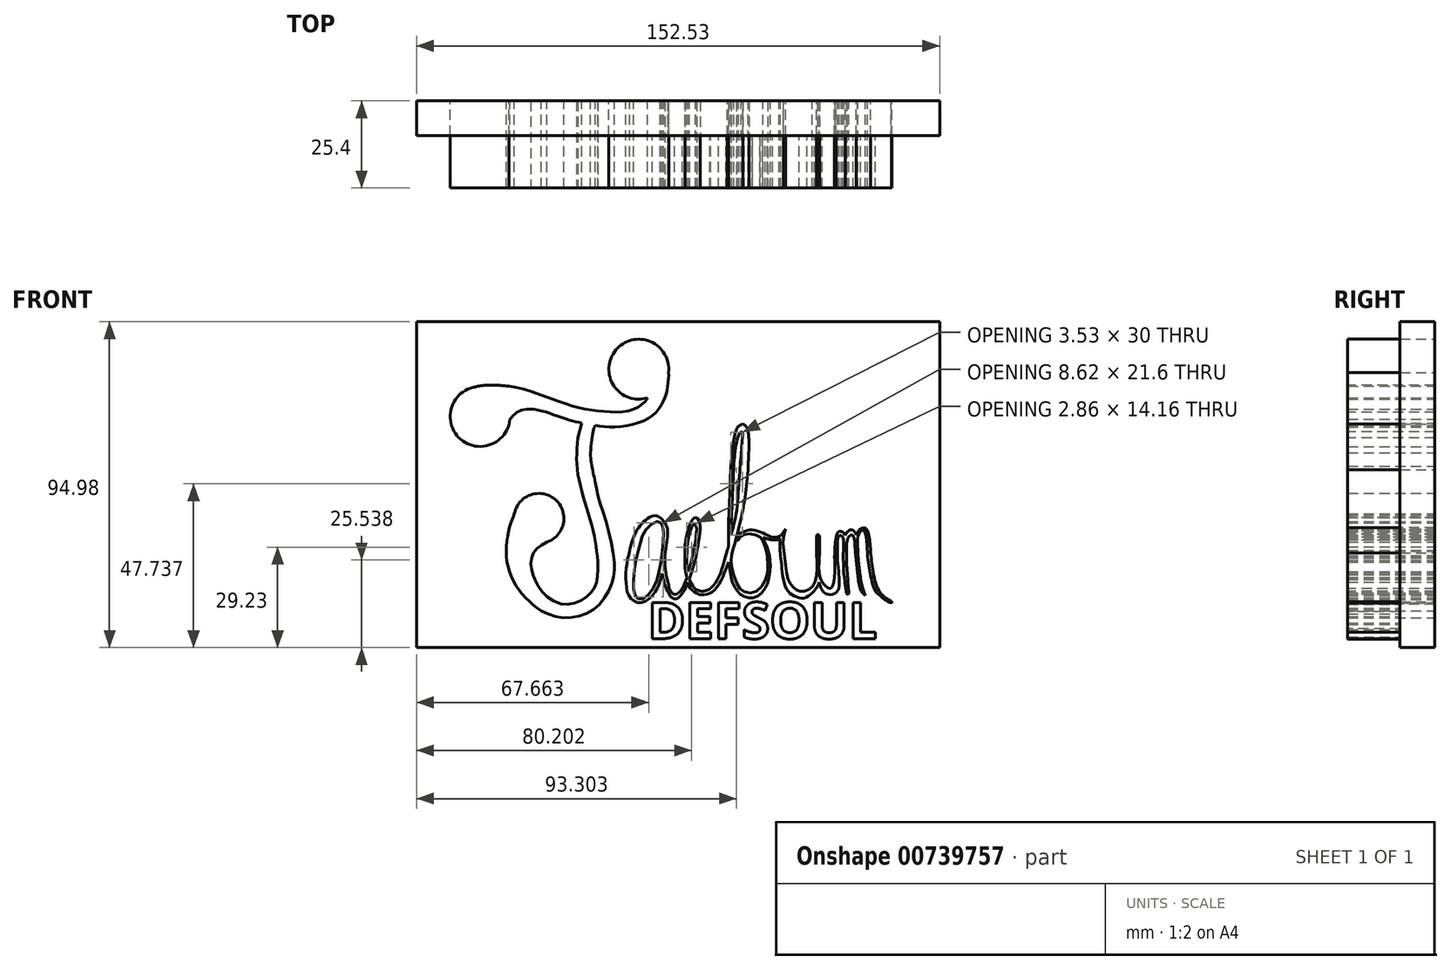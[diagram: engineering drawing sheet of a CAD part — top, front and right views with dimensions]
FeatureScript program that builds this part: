
annotation { "Feature Type Name" : "Feature", "Feature Type Description" : "" }
export const myFeature = defineFeature(function(context is Context, id is Id, definition is map)
    precondition{}
    {
        {
            var Q0;
            Q0=qCreatedBy(makeId("Front.planeOp"),FACE);
            var sketch = newSketch(context, id + "F0", { "sketchPlane" : qUnion([Q0])});
            skCircle(sketch, "E0", {"center": v(-57.58, 28.36) * mm, "radius": 8.73 * mm});
            skFitSpline(sketch, "E1", {"points": [v(-55.56, 36.85) * mm, v(-47.7, 37) * mm, v(-31.6, 31.7) * mm, v(-22.02, 29.91) * mm, v(-13.64, 30.17) * mm, v(-9.36, 32.82) * mm, v(-8.72, 33.82) * mm], "startDerivative": vector(35.06, 6.54) * mm, "endDerivative": vector(6.2, 15.4) * mm});
            skFitSpline(sketch, "E2", {"points": [v(-48.89, 27.54) * mm, v(-46.41, 29.83) * mm, v(-41.2, 30.34) * mm, v(-31.95, 27.43) * mm, v(-26.13, 26.15) * mm, v(-19.29, 25.3) * mm, v(-8.72, 27.69) * mm, v(-4.23, 32.65) * mm, v(-2.86, 37.36) * mm, v(-2.66, 41.14) * mm], "startDerivative": vector(25.7, 30.9) * mm, "endDerivative": vector(-3.63, 27.27) * mm});
            skCircle(sketch, "E3", {"center": v(-11.33, 42.15) * mm, "radius": 8.73 * mm});
            skCircle(sketch, "E4", {"center": v(-40.44, -1.35) * mm, "radius": 7.28 * mm});
            skFitSpline(sketch, "E5", {"points": [v(-47.6, 0) * mm, v(-48.78, -3.23) * mm, v(-49.93, -9.63) * mm, v(-49.07, -16.75) * mm, v(-45.3, -23.43) * mm, v(-39.82, -28.32) * mm], "startDerivative": vector(-8.2, -19.78) * mm, "endDerivative": vector(26.77, -20.88) * mm});
            skFitSpline(sketch, "E6", {"points": [v(-39.82, -28.32) * mm, v(-33.9, -30.27) * mm, v(-27.59, -29.45) * mm, v(-22.3, -25.9) * mm, v(-19.14, -20) * mm, v(-18.43, -15.1) * mm, v(-20.16, -4.83) * mm, v(-23, 4.53) * mm, v(-24.03, 9.11) * mm], "startDerivative": vector(48.48, -21.15) * mm, "endDerivative": vector(-7.56, 40.7) * mm});
            skFitSpline(sketch, "E7", {"points": [v(-38.08, -8.25) * mm, v(-41.75, -11.04) * mm, v(-42.75, -14.8) * mm, v(-41.75, -18.87) * mm, v(-38.37, -23.96) * mm, v(-31.66, -26.45) * mm, v(-26.14, -23.8) * mm, v(-23.76, -20.5) * mm, v(-23.27, -13.83) * mm], "startDerivative": vector(-36.38, -20.88) * mm, "endDerivative": vector(-0.7, 52.44) * mm});
            skFitSpline(sketch, "E8", {"points": [v(-23.27, -13.83) * mm, v(-24.45, -5.8) * mm, v(-27.36, 4.53) * mm, v(-29.33, 13.72) * mm, v(-29.07, 22.1) * mm], "startDerivative": vector(-3.51, 32.96) * mm, "endDerivative": vector(3.07, 34.87) * mm});
            skFitSpline(sketch, "E9", {"points": [v(-29.07, 22.1) * mm, v(-28.21, 25.28) * mm, v(-27.9, 26.47) * mm], "startDerivative": vector(1.55, 5.76) * mm, "endDerivative": vector(0.75, 2.81) * mm});
            skFitSpline(sketch, "E10", {"points": [v(-24.03, 9.11) * mm, v(-24.89, 13.55) * mm, v(-25.37, 17.66) * mm, v(-24.65, 23.95) * mm, v(-24.03, 25.75) * mm], "startDerivative": vector(-3.38, 17.42) * mm, "endDerivative": vector(3.65, 8.4) * mm});
            skFitSpline(sketch, "E11", {"points": [v(-4.9, -2.66) * mm, v(-6.19, -2.3) * mm, v(-9.36, -4.75) * mm, v(-10.8, -8.2) * mm, v(-12.16, -13.83) * mm, v(-12.88, -21.51) * mm, v(-12.09, -24.25) * mm, v(-10.58, -24.97) * mm, v(-7.63, -22.38) * mm, v(-5.54, -17.41) * mm, v(-4.23, -8.78) * mm, v(-4.23, -4.25) * mm, v(-4.9, -2.66) * mm]});
            skFitSpline(sketch, "E12", {"points": [v(-5.1, -1.08) * mm, v(-6.27, -0.56) * mm, v(-8.03, -1) * mm, v(-10.98, -3.49) * mm, v(-12.86, -6.87) * mm, v(-14, -10.76) * mm], "startDerivative": vector(-8.28, 5.07) * mm, "endDerivative": vector(-4.26, -16.62) * mm});
            skFitSpline(sketch, "E13", {"points": [v(-14, -10.76) * mm, v(-14.9, -15.18) * mm, v(-15.04, -20.5) * mm, v(-14, -24.25) * mm, v(-11.3, -25.9) * mm, v(-7.63, -24.25) * mm, v(-5.54, -20.72) * mm, v(-4.53, -17.41) * mm], "startDerivative": vector(-6.8, -28.21) * mm, "endDerivative": vector(6.65, 24.7) * mm});
            skFitSpline(sketch, "E14", {"points": [v(-5.1, -1.08) * mm, v(-3.24, -3.45) * mm, v(-3.02, -7.27) * mm, v(-3.74, -13.24) * mm, v(-2.8, -20) * mm], "startDerivative": vector(11.2, -10.92) * mm, "endDerivative": vector(6.02, -22.76) * mm});
            skFitSpline(sketch, "E15", {"points": [v(-2.8, -20) * mm, v(-2.01, -22.6) * mm, v(-0.72, -23.53) * mm, v(1, -22.23) * mm, v(2.52, -19.14) * mm], "startDerivative": vector(2.08, -10.74) * mm, "endDerivative": vector(4.4, 11.1) * mm});
            skFitSpline(sketch, "E16", {"points": [v(-4.53, -17.41) * mm, v(-3.78, -20.37) * mm, v(-2.8, -22.82) * mm, v(-1.9, -24.25) * mm, v(-0.49, -24.84) * mm, v(0.82, -23.88) * mm, v(2.54, -21.21) * mm, v(2.93, -20) * mm], "startDerivative": vector(3.81, -17.35) * mm, "endDerivative": vector(2.15, 9.7) * mm});
            skFitSpline(sketch, "E17", {"points": [v(2.52, -19.14) * mm, v(2.78, -18.5) * mm], "startDerivative": vector(0.26, 0.64) * mm, "endDerivative": vector(0.26, 0.64) * mm});
            skFitSpline(sketch, "E18", {"points": [v(2.78, -18.5) * mm, v(2.35, -17.05) * mm, v(2.11, -14.4) * mm, v(2.13, -11.06) * mm, v(2.2, -9.66) * mm], "startDerivative": vector(-2.3, 6.45) * mm, "endDerivative": vector(0.39, 6.1) * mm});
            skFitSpline(sketch, "E19", {"points": [v(2.2, -9.66) * mm, v(2.2, -8.52) * mm, v(3.44, -3.59) * mm, v(4.74, -1.35) * mm, v(5.7, -1.23) * mm, v(6.53, -3.05) * mm, v(6.4, -6.13) * mm, v(5.65, -10.82) * mm, v(5.26, -12.94) * mm], "startDerivative": vector(-1.12, 10.68) * mm, "endDerivative": vector(-3.09, -16.08) * mm});
            skFitSpline(sketch, "E20", {"points": [v(3.41, -19.07) * mm, v(4.41, -15.96) * mm, v(5.26, -12.94) * mm], "startDerivative": vector(2.04, 6.18) * mm, "endDerivative": vector(1.64, 6.09) * mm});
            skFitSpline(sketch, "E21", {"points": [v(3.41, -19.07) * mm, v(4.9, -21.67) * mm, v(7.44, -22.55) * mm, v(10.55, -20.83) * mm, v(13.15, -15.44) * mm, v(14.42, -10.63) * mm], "startDerivative": vector(6.77, -16.8) * mm, "endDerivative": vector(4.83, 20.57) * mm});
            skFitSpline(sketch, "E22", {"points": [v(2.93, -20) * mm, v(3.41, -21.37) * mm, v(5.26, -23.06) * mm, v(6.44, -23.58) * mm, v(8.43, -23.52) * mm, v(11.28, -21.73) * mm, v(13.82, -16.68) * mm, v(14.82, -14.14) * mm], "startDerivative": vector(2.14, -12.7) * mm, "endDerivative": vector(5.95, 15.05) * mm});
            skFitSpline(sketch, "E23", {"points": [v(3.03, -16.85) * mm, v(2.68, -14.88) * mm, v(2.73, -11.5) * mm, v(3.03, -7.74) * mm, v(4.41, -3.42) * mm, v(5.17, -2.69) * mm], "startDerivative": vector(-2.54, 10.73) * mm, "endDerivative": vector(6.08, 3.92) * mm});
            skFitSpline(sketch, "E24", {"points": [v(3.03, -16.85) * mm, v(3.97, -13.9) * mm, v(5.17, -7.9) * mm, v(5.5, -4.19) * mm, v(5.17, -2.69) * mm], "startDerivative": vector(3.96, 11.02) * mm, "endDerivative": vector(-2.64, 8.1) * mm});
            skFitSpline(sketch, "E25", {"points": [v(14.42, -10.63) * mm, v(14.82, -9.56) * mm, v(14.82, -7.15) * mm, v(14.82, -2.31) * mm], "startDerivative": vector(2.16, 4.38) * mm, "endDerivative": vector(0.16, 11.32) * mm});
            skFitSpline(sketch, "E26", {"points": [v(14.82, -2.31) * mm, v(15.25, 6.48) * mm, v(15.51, 13.63) * mm, v(15.68, 15.77) * mm], "startDerivative": vector(1.16, 20.86) * mm, "endDerivative": vector(0.87, 8.82) * mm});
            skFitSpline(sketch, "E27", {"points": [v(15.68, 15.77) * mm, v(16.1, 19.5) * mm, v(17.4, 25.03) * mm, v(19, 26.12) * mm], "startDerivative": vector(1, 9.76) * mm, "endDerivative": vector(7.17, 2.57) * mm});
            skFitSpline(sketch, "E28", {"points": [v(19, 26.12) * mm, v(19.93, 25.48) * mm, v(20.75, 22.16) * mm, v(20.66, 16.32) * mm, v(20.5, 12.9) * mm], "startDerivative": vector(6.8, -2.85) * mm, "endDerivative": vector(-0.49, -12.18) * mm});
            skFitSpline(sketch, "E29", {"points": [v(20.5, 12.9) * mm, v(19.5, 3.89) * mm, v(18.28, -2.31) * mm, v(15.68, -12.17) * mm], "startDerivative": vector(-2.72, -27.76) * mm, "endDerivative": vector(-7.83, -28.82) * mm});
            skFitSpline(sketch, "E30", {"points": [v(15.68, -12.17) * mm, v(15.68, -14.92) * mm, v(17.45, -20.78) * mm, v(19.33, -22.65) * mm, v(22.78, -22.73) * mm, v(25.55, -19.42) * mm, v(26.23, -16.85) * mm, v(26.23, -13.55) * mm, v(25.87, -10.93) * mm, v(24.76, -7.76) * mm, v(23.5, -6.46) * mm, v(20.15, -5.89) * mm, v(18.5, -6.54) * mm, v(17.81, -7.54) * mm], "startDerivative": vector(-3.16, -31.7) * mm, "endDerivative": vector(-11.45, -21.77) * mm});
            skFitSpline(sketch, "E31", {"points": [v(14.82, -14.14) * mm, v(15.62, -18.66) * mm, v(17.17, -22.3) * mm, v(19.8, -24.24) * mm, v(23.32, -24.02) * mm, v(26.27, -20) * mm, v(26.99, -14.52) * mm, v(26.38, -10.63) * mm, v(24.83, -6.86) * mm], "startDerivative": vector(5, -35.2) * mm, "endDerivative": vector(-14.17, 30.67) * mm});
            skFitSpline(sketch, "E32", {"points": [v(17.81, -7.54) * mm, v(17.64, -7.7) * mm, v(17.28, -7.67) * mm, v(17.17, -7.4) * mm, v(17.37, -6.94) * mm], "startDerivative": vector(-0.63, -0.96) * mm, "endDerivative": vector(0.93, 1.56) * mm});
            skFitSpline(sketch, "E33", {"points": [v(17.37, -6.94) * mm, v(18.22, -5.8) * mm, v(20.18, -4.9) * mm, v(22.39, -4.81) * mm, v(25.25, -5.78) * mm, v(26.8, -6.55) * mm, v(28.65, -6.86) * mm, v(30.37, -6.06) * mm, v(30.8, -5.37) * mm], "startDerivative": vector(6.05, 11.03) * mm, "endDerivative": vector(3.5, 8.22) * mm});
            skFitSpline(sketch, "E34", {"points": [v(24.83, -6.86) * mm, v(26.06, -7.28) * mm, v(27.6, -7.63) * mm, v(28.86, -7.61) * mm, v(29.62, -7.43) * mm], "startDerivative": vector(4.59, -1.63) * mm, "endDerivative": vector(3.53, 1.03) * mm});
            skLineSegment(sketch, "E35", {"start": v(29.62, -7.43) * mm, "end": v(29.9, -7.13) * mm});
            skFitSpline(sketch, "E36", {"points": [v(29.9, -7.13) * mm, v(29.82, -8.2) * mm, v(29.8, -10.08) * mm, v(29.9, -11.35) * mm], "startDerivative": vector(-0.34, -3.32) * mm, "endDerivative": vector(0.36, -3.7) * mm});
            skFitSpline(sketch, "E37", {"points": [v(29.9, -11.35) * mm, v(30.39, -15.89) * mm, v(31.72, -21.9) * mm, v(34.17, -24.02) * mm, v(36.8, -24.6) * mm, v(39.2, -23.12) * mm], "startDerivative": vector(2.01, -19.12) * mm, "endDerivative": vector(13.47, 11.42) * mm});
            skFitSpline(sketch, "E38", {"points": [v(30.8, -5.37) * mm, v(31.45, -4.48) * mm], "startDerivative": vector(0.66, 0.9) * mm, "endDerivative": vector(0.66, 0.9) * mm});
            skFitSpline(sketch, "E39", {"points": [v(31.45, -4.48) * mm, v(30.8, -7.13) * mm, v(31.23, -13.3) * mm, v(32.4, -19.54) * mm, v(34.36, -22.02) * mm, v(36.07, -22.66) * mm, v(38.81, -21.72) * mm, v(40.57, -17.83) * mm, v(40.52, -11.35) * mm, v(40.44, -6.7) * mm], "startDerivative": vector(-9.47, -26.13) * mm, "endDerivative": vector(0, 37.12) * mm});
            skFitSpline(sketch, "E40", {"points": [v(39.2, -23.12) * mm, v(40.65, -21.34) * mm, v(41.2, -20) * mm], "startDerivative": vector(2.97, 3.25) * mm, "endDerivative": vector(0.96, 3) * mm});
            skFitSpline(sketch, "E41", {"points": [v(40.44, -6.7) * mm, v(40.54, -6.28) * mm, v(40.9, -6.1) * mm, v(41.26, -6.26) * mm, v(41.33, -7.02) * mm], "startDerivative": vector(0.17, 1.99) * mm, "endDerivative": vector(-0.16, -2.84) * mm});
            skFitSpline(sketch, "E42", {"points": [v(41.33, -7.02) * mm, v(41.33, -11.8) * mm, v(41.33, -17.83) * mm, v(42.71, -20.6) * mm, v(44.4, -21.77) * mm, v(45.46, -20) * mm, v(45.77, -12.31) * mm], "startDerivative": vector(0.62, -24.76) * mm, "endDerivative": vector(-0.76, 37.6) * mm});
            skFitSpline(sketch, "E43", {"points": [v(41.2, -20) * mm, v(42.1, -22.23) * mm, v(43.78, -23.5) * mm, v(46.27, -22.9) * mm, v(47.14, -20) * mm, v(46.58, -13.55) * mm], "startDerivative": vector(4.1, -13.6) * mm, "endDerivative": vector(-3.08, 24.18) * mm});
            skFitSpline(sketch, "E44", {"points": [v(45.77, -12.31) * mm, v(45.97, -8.42) * mm, v(46.22, -6.83) * mm], "startDerivative": vector(0.23, 7.1) * mm, "endDerivative": vector(0.72, 3.6) * mm});
            skFitSpline(sketch, "E45", {"points": [v(15.42, -6.26) * mm, v(17, -0.44) * mm, v(18.02, 11) * mm, v(18.56, 17.77) * mm], "startDerivative": vector(6.01, 17.67) * mm, "endDerivative": vector(1.77, 19.83) * mm});
            skFitSpline(sketch, "E46", {"points": [v(18.56, 17.77) * mm, v(18.91, 22.16) * mm, v(18.91, 23.57) * mm, v(18.56, 23.88) * mm, v(17.74, 22.76) * mm, v(16.8, 18.44) * mm, v(16.32, 13.9) * mm], "startDerivative": vector(1.59, 21.96) * mm, "endDerivative": vector(-1.8, -19.48) * mm});
            skFitSpline(sketch, "E47", {"points": [v(16.32, 13.9) * mm, v(15.42, -6.26) * mm], "startDerivative": vector(-0.9, -20.17) * mm, "endDerivative": vector(-0.9, -20.17) * mm});
            skFitSpline(sketch, "E48", {"points": [v(46.58, -13.55) * mm, v(46.58, -9.55) * mm, v(46.87, -6.72) * mm, v(47.74, -6.26) * mm], "startDerivative": vector(0.06, 9.29) * mm, "endDerivative": vector(4.72, 1.1) * mm});
            skFitSpline(sketch, "E49", {"points": [v(46.22, -6.83) * mm, v(46.87, -5.27) * mm, v(48, -5.27) * mm, v(48.86, -6.26) * mm], "startDerivative": vector(1.1, 5.22) * mm, "endDerivative": vector(2.23, -3.6) * mm});
            skFitSpline(sketch, "E50", {"points": [v(47.74, -6.26) * mm, v(48.25, -7.13) * mm, v(48.3, -11.28) * mm, v(48.45, -17.83) * mm], "startDerivative": vector(3.33, -3.8) * mm, "endDerivative": vector(0.66, -14.56) * mm});
            skFitSpline(sketch, "E51", {"points": [v(48.45, -17.83) * mm, v(49.16, -22.7) * mm, v(49.37, -23.4) * mm, v(49.6, -23.5) * mm, v(49.85, -23.2) * mm, v(49.77, -21.9) * mm, v(49.68, -19.88) * mm, v(49.65, -19.22) * mm], "startDerivative": vector(2.83, -20.12) * mm, "endDerivative": vector(-0.38, 5.14) * mm});
            skFitSpline(sketch, "E52", {"points": [v(48.86, -6.26) * mm, v(49.9, -4.9) * mm, v(51.16, -4.81) * mm, v(52.1, -6.26) * mm], "startDerivative": vector(2.5, 4.65) * mm, "endDerivative": vector(2.15, -5.16) * mm});
            skFitSpline(sketch, "E53", {"points": [v(52.1, -6.26) * mm, v(52.8, -4.9) * mm, v(53.88, -4.16) * mm, v(55.01, -4.4) * mm, v(55.93, -7.29) * mm, v(56.3, -11.44) * mm], "startDerivative": vector(3.45, 8.55) * mm, "endDerivative": vector(0.98, -14.7) * mm});
            skFitSpline(sketch, "E54", {"points": [v(49.27, -10.87) * mm, v(49.4, -8.04) * mm, v(50.3, -6.34) * mm, v(51.15, -6.34) * mm, v(51.69, -9.34) * mm, v(51.96, -12.5) * mm], "startDerivative": vector(-0.45, 13.01) * mm, "endDerivative": vector(1.26, -12.43) * mm});
            skFitSpline(sketch, "E55", {"points": [v(52.58, -12.5) * mm, v(52.58, -12.09) * mm, v(52.51, -9.75) * mm, v(52.42, -7.5) * mm, v(53.12, -5.32) * mm, v(53.93, -4.81) * mm, v(54.38, -4.9) * mm, v(55.21, -9.28) * mm, v(55.4, -12.5) * mm], "startDerivative": vector(0.03, 5.32) * mm, "endDerivative": vector(0.51, -16.5) * mm});
            skFitSpline(sketch, "E56", {"points": [v(49.27, -10.87) * mm, v(49.27, -14.66) * mm, v(49.65, -19.22) * mm], "startDerivative": vector(-0.17, -7.77) * mm, "endDerivative": vector(0.9, -8.91) * mm});
            skFitSpline(sketch, "E57", {"points": [v(51.96, -12.5) * mm, v(52.53, -18.05) * mm, v(53.38, -22.22) * mm, v(54.7, -23.85) * mm], "startDerivative": vector(1.4, -13.9) * mm, "endDerivative": vector(6, -5.54) * mm});
            skFitSpline(sketch, "E58", {"points": [v(52.58, -12.5) * mm, v(53.04, -16.84) * mm, v(53.92, -21.7) * mm, v(54.7, -23.85) * mm], "startDerivative": vector(1.07, -11.57) * mm, "endDerivative": vector(3.13, -7.25) * mm});
            skFitSpline(sketch, "E59", {"points": [v(55.4, -12.5) * mm, v(56.34, -18.42) * mm, v(57.93, -22.78) * mm, v(61.27, -25.58) * mm, v(62.2, -25.94) * mm], "startDerivative": vector(2.9, -19.26) * mm, "endDerivative": vector(6, -1.63) * mm});
            skFitSpline(sketch, "E60", {"points": [v(56.3, -11.44) * mm, v(56.77, -15.6) * mm, v(57.82, -20.43) * mm, v(59.22, -23.14) * mm, v(60.8, -24.61) * mm, v(62.35, -25.58) * mm], "startDerivative": vector(1.64, -17.34) * mm, "endDerivative": vector(10.16, -5.93) * mm});
            skFitSpline(sketch, "E61", {"points": [v(62.2, -25.94) * mm, v(62.41, -25.94) * mm, v(62.53, -25.76) * mm, v(62.35, -25.58) * mm], "startDerivative": vector(0.66, -0.15) * mm, "endDerivative": vector(-0.72, 0.44) * mm});
            skFitSpline(sketch, "E62", {"points": [v(-59.66, 36.83) * mm, v(-55.83, 37.48) * mm, v(-49.15, 37.2) * mm], "startDerivative": vector(8.22, 1.95) * mm, "endDerivative": vector(12.6, -1.08) * mm});
            skSolve(sketch);
        }
        {
            var Q0;
            {var subQ0=sQuery(id+"F0.wireOp",EDGE,"E0");var subQ1=makeQuery(id+"F0.imprint","INTERSECT",VERTEX,{"derivedFrom":[subQ0,sQuery(id+"F0.wireOp",EDGE,"E1")]});Q0=makeQuery(id+"F0.imprint","IMPRINT",FACE,{"disambiguationData":[TD([[makeQuery(id+"F0.imprint","IMPRINT",EDGE,{"disambiguationData":[TD([[subQ1,-1.0]])],"derivedFrom":subQ0}),1.0]])]});}
            var Q1;
            {var subQ1=sQuery(id+"F0.wireOp",EDGE,"E0");var subQ5=sQuery(id+"F0.wireOp",EDGE,"E1");var subQ10=makeQuery(id+"F0.imprint","INTERSECT",VERTEX,{"derivedFrom":[subQ1,subQ5]});Q1=makeQuery(id+"F0.imprint","IMPRINT",FACE,{"disambiguationData":[TD([[makeQuery(id+"F0.imprint","IMPRINT",EDGE,{"disambiguationData":[TD([[subQ10,1.0]])],"derivedFrom":subQ1}),-1.0]])]});}
            var Q2;
            {var subQ0=sQuery(id+"F0.wireOp",EDGE,"E3");var subQ1=makeQuery(id+"F0.imprint","INTERSECT",VERTEX,{"derivedFrom":[sQuery(id+"F0.wireOp",EDGE,"E1"),subQ0]});Q2=makeQuery(id+"F0.imprint","IMPRINT",FACE,{"disambiguationData":[TD([[makeQuery(id+"F0.imprint","IMPRINT",EDGE,{"disambiguationData":[TD([[subQ1,-1.0]])],"derivedFrom":subQ0}),1.0]])]});}
            var Q3;
            {var subQ0=sQuery(id+"F0.wireOp",EDGE,"E1");var subQ1=sQuery(id+"F0.wireOp",EDGE,"E0");var subQ2=makeQuery(id+"F0.imprint","INTERSECT",VERTEX,{"derivedFrom":[subQ1,subQ0]});Q3=makeQuery(id+"F0.imprint","IMPRINT",FACE,{"disambiguationData":[TD([[makeQuery(id+"F0.imprint","IMPRINT",EDGE,{"disambiguationData":[TD([[subQ2,-1.0]])],"derivedFrom":subQ1}),-1.0]])]});}
            var Q4;
            {var subQ0=sQuery(id+"F0.wireOp",EDGE,"E4");var subQ1=makeQuery(id+"F0.imprint","INTERSECT",VERTEX,{"derivedFrom":[subQ0,sQuery(id+"F0.wireOp",EDGE,"E5")]});Q4=makeQuery(id+"F0.imprint","IMPRINT",FACE,{"disambiguationData":[TD([[makeQuery(id+"F0.imprint","IMPRINT",EDGE,{"disambiguationData":[TD([[subQ1,-1.0]])],"derivedFrom":subQ0}),1.0]])]});}
            var Q5;
            {var subQ0=sQuery(id+"F0.wireOp",EDGE,"E5");Q5=makeQuery(id+"F0.imprint","IMPRINT",FACE,{"disambiguationData":[TD([[makeQuery(id+"F0.imprint","IMPRINT",EDGE,{"derivedFrom":subQ0}),1.0]])]});}
            var Q6;
            Q6=makeQuery(id+"F0.imprint","IMPRINT",FACE,{"disambiguationData":[TD([[makeQuery(id+"F0.imprint","IMPRINT",EDGE,{"derivedFrom":sQuery(id+"F0.wireOp",EDGE,"E11")}),-1.0]])]});
            extrude(context, id + "F1", {"entities" : qUnion([Q0, Q1, Q2, Q3, Q4, Q5, Q6]), "depth" : 25.4 * mm, "offsetDistance" : 25.4 * mm});
        }
        {
            var Q0;
            Q0=qCreatedBy(makeId("Front.planeOp"),FACE);
            var sketch = newSketch(context, id + "F2", { "sketchPlane" : qUnion([Q0])});
            skLineSegment(sketch, "E63.bottom", {"start": v(-76.12, 55.98) * mm, "end": v(76.41, 55.98) * mm});
            skLineSegment(sketch, "E63.top", {"start": v(-76.12, -39) * mm, "end": v(76.41, -39) * mm});
            skLineSegment(sketch, "E63.left", {"start": v(-76.12, 55.98) * mm, "end": v(-76.12, -39) * mm});
            skLineSegment(sketch, "E63.right", {"start": v(76.41, 55.98) * mm, "end": v(76.41, -39) * mm});
            skSolve(sketch);
        }
        {
            var Q0;
            Q0=makeQuery(id+"F2.imprint","IMPRINT",FACE,{"disambiguationData":[TD([[makeQuery(id+"F2.imprint","IMPRINT",EDGE,{"derivedFrom":sQuery(id+"F2.wireOp",EDGE,"E63.bottom")}),-1.0]])]});
            extrude(context, id + "F3", {"entities" : qUnion([Q0]), "depth" : 10.16 * mm, "offsetDistance" : 25.4 * mm});
        }
        {
            var Q0;
            Q0=qCreatedBy(makeId("Front.planeOp"),FACE);
            var sketch = newSketch(context, id + "F4", { "sketchPlane" : qUnion([Q0])});
            skText(sketch, "E64", { "text": "DEFSOUL", "fontName": "OpenSans-Bold.ttf"});
            const initialGuessF4  = {"E64": [-0.00867, -0.0364, 1, 0, 0.01065]};
            skSetInitialGuess(sketch, initialGuessF4);
            skSolve(sketch);
        }
        {
            var Q0;
            Q0 = qSketchRegion(id + "F4", true);
            extrude(context, id + "F5", {"entities" : qUnion([Q0]), "operationType" : NewBodyOperationType.ADD, "depth" : 25.4 * mm, "offsetDistance" : 25.4 * mm});
        }
    });
